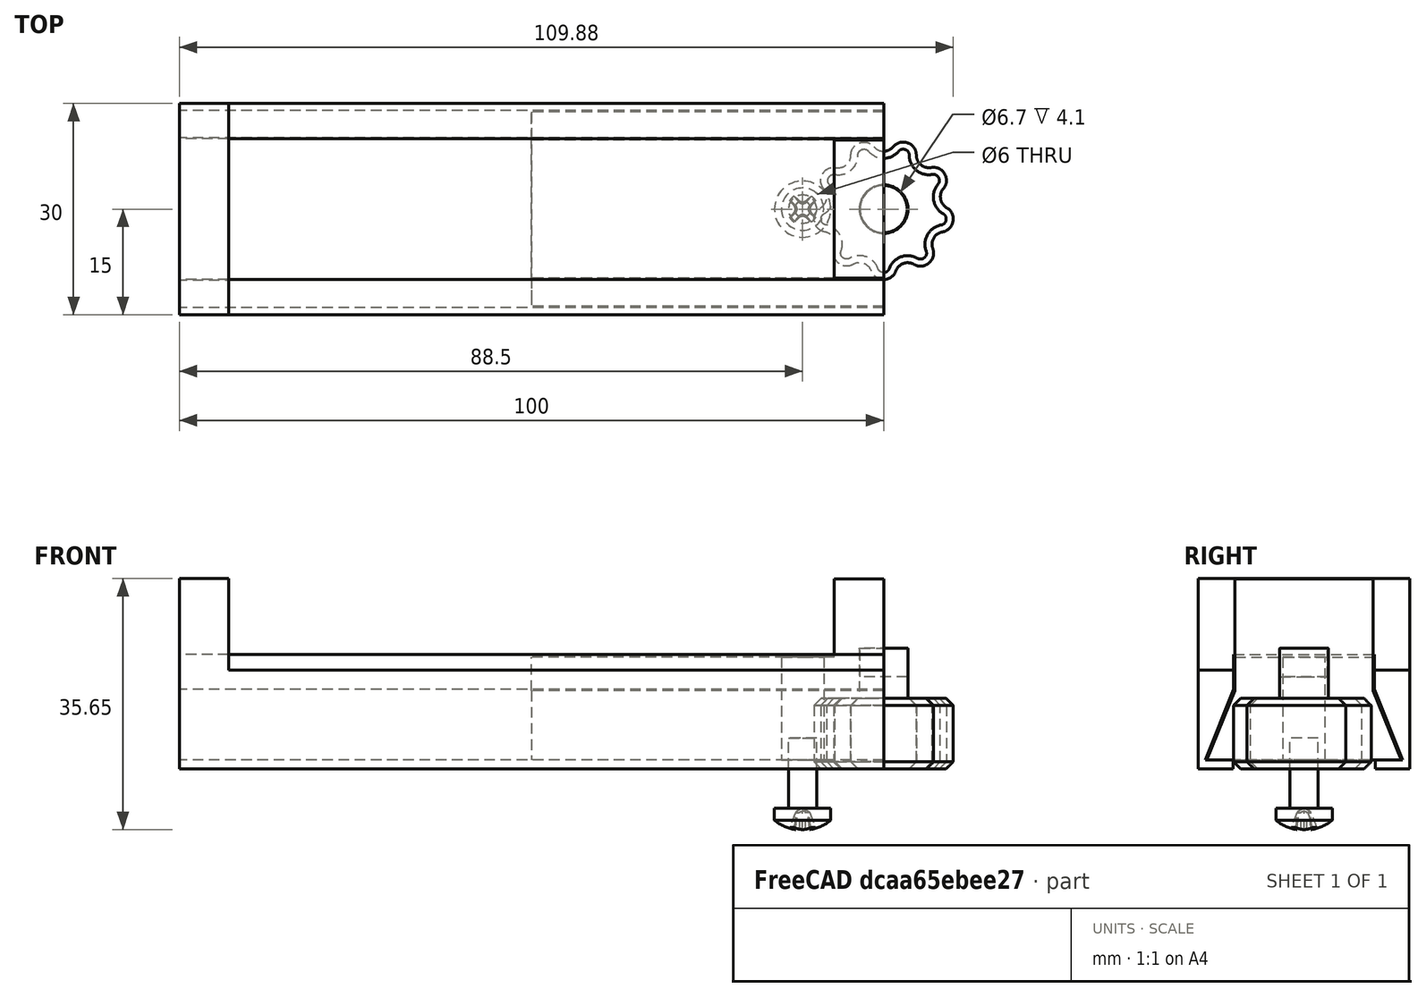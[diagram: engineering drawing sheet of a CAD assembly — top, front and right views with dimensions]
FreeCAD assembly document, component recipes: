
FREECAD ASSEMBLY — COMPONENT RECIPES ("USBCPhoneHolder - 04022025")

This assembly document has 4 components, labeled P0..P3 below (a component is one placed body or linked part). 4 of them carry a construction recipe — the FreeCAD feature program that regenerates the part from scratch, quoted from this document or its linked companion documents; the rest are supplied as boundary geometry only. No exploded tour is included for this assembly.
COMPONENT P0 — recipe-attached ("PhoneClampLeftStationary", modeled in this document).
Construction recipe (the document's own serialized feature program — sketch geometry with constraints, then the solid features built on it; lengths are millimeters unless a unit is written):

FEATURE [Sketcher::SketchObject] Sketch
  ArcFitTolerance = 1e-06
  FullyConstrained = true
  MakeInternals = false
  expr: Constraints[2] = Spreadsheet001.PhoneClampWidth
  expr: Constraints[3] = Spreadsheet001.PhoneClampHeight
  sketch-geometry (7):
    g0: LineSegment StartX=0 StartY=-15 StartZ=0 EndX=0 EndY=15 EndZ=0
    g1: LineSegment StartX=-100 StartY=15 StartZ=0 EndX=-100 EndY=-15 EndZ=0
    g2: LineSegment StartX=-93 StartY=15 StartZ=0 EndX=-93 EndY=-15 EndZ=0
    g3: LineSegment StartX=-100 StartY=15 StartZ=0 EndX=-93 EndY=15 EndZ=0
    g4: LineSegment StartX=-93 StartY=15 StartZ=0 EndX=0 EndY=15 EndZ=0
    g5: LineSegment StartX=-100 StartY=-15 StartZ=0 EndX=-93 EndY=-15 EndZ=0
    g6: LineSegment StartX=-93 StartY=-15 StartZ=0 EndX=0 EndY=-15 EndZ=0
  constraints (19):
    c: Vertical(g0)
    c: Vertical(g1)
    c: DistanceX(g1,g0) = 100
    c: DistanceY(g0,g0) = 30
    c: Symmetric(g0,g0,g-1)
    c: Vertical(g2)
    c: DistanceX(g1,g2) = 7  'LengthOfClip'
    c: Coincident(g3,g1)
    c: Coincident(g3,g2)
    c: Horizontal(g3)
    c: Coincident(g4,g2)
    c: Coincident(g4,g0)
    c: Horizontal(g4)
    c: Coincident(g5,g1)
    c: Coincident(g5,g2)
    c: Horizontal(g5)
    c: Coincident(g6,g2)
    c: Coincident(g6,g0)
    c: Horizontal(g6)
FEATURE [PartDesign::Pad] Pad
  Direction = (0,0,1)
  Length = 14
  Length2 = 10
  Profile = -> Sketch [Edge2,Edge5,Edge3,Edge7,Edge4,Edge1]
  ReferenceAxis = -> Sketch [N_Axis]
  Refine = true
  Suppressed = false
  Type = 0
  expr: Length = Spreadsheet001.PhoneClampDepth
FEATURE [PartDesign::Pad] Pad001  label="LeftBody"
  BaseFeature = -> Pad
  Direction = (0,0,1)
  Length = 27.02
  Length2 = 10
  Profile = -> Sketch [Edge6,Edge5,Edge3,Edge4]
  ReferenceAxis = -> Sketch [N_Axis]
  Refine = true
  Suppressed = false
  Type = 0
  expr: Length = Spreadsheet001.PhoneClampDepth * 1.93
FEATURE [PartDesign::Boolean] Boolean
  BaseFeature = -> Pad001
  Group = -> [Body001]
  Refine = true
  Suppressed = false
  Type = 1
  UsePlacement = true
FEATURE [Sketcher::SketchObject] Sketch007  label="BottomRemoval"
  ArcFitTolerance = 1e-06
  AttachmentSupport = -> [Boolean]
  FullyConstrained = true
  MakeInternals = false
  MapMode = 5
  Placement = pos=(0,0,0) rot=(0.57735,0.57735,0.57735;2.0944rad)
  expr: Constraints[15] = <<ProfileStationaryCut>>.Constraints.OffsetFromBottom
  expr: Constraints[16] = Spreadsheet001.KnobDiameter / 2 + Spreadsheet.PLA / 2
  sketch-geometry (6):
    g0: LineSegment StartX=0 StartY=0 StartZ=0 EndX=-10.1 EndY=0 EndZ=0
    g1: LineSegment StartX=-10.1 StartY=0 StartZ=0 EndX=-10.1 EndY=1.29 EndZ=0
    g2: LineSegment StartX=-10.1 StartY=1.29 StartZ=0 EndX=0 EndY=1.29 EndZ=0
    g3: LineSegment StartX=0 StartY=1.29 StartZ=0 EndX=10.1 EndY=1.29 EndZ=0
    g4: LineSegment StartX=10.1 StartY=1.29 StartZ=0 EndX=10.1 EndY=0 EndZ=0
    g5: LineSegment StartX=10.1 StartY=0 StartZ=0 EndX=0 EndY=0 EndZ=0
  constraints (17):
    c: Coincident(g0,g-1)
    c: PointOnObject(g0,g-1)
    c: Coincident(g1,g0)
    c: Vertical(g1)
    c: Coincident(g2,g1)
    c: PointOnObject(g2,g-2)
    c: Horizontal(g2)
    c: Coincident(g3,g2)
    c: Horizontal(g3)
    c: Coincident(g4,g3)
    c: PointOnObject(g4,g-1)
    c: Vertical(g4)
    c: Coincident(g5,g4)
    c: Coincident(g5,g0)
    c: Equal(g0,g5)
    c: DistanceY(g1,g1) = 1.29
    c: DistanceX(g0,g0) = 10.1
FEATURE [PartDesign::Pocket] Pocket001  label="HoleBottom"
  BaseFeature = -> Boolean
  Direction = (-1,0,0)
  Length = 5
  Length2 = 5
  Profile = -> Sketch007
  ReferenceAxis = -> Sketch007 [N_Axis]
  Refine = true
  Suppressed = false
  Type = 1
FEATURE [PartDesign::Body] Body  label="PhoneClampLeftStationary"
  AllowCompound = false
  Group = -> [Sketch,Pad,Pad001,Boolean,Sketch007,Pocket001]
  Origin = -> Origin
  Tip = -> Pocket001
COMPONENT P1 — recipe-attached ("PhoneClampSubtract", modeled in this document).
Construction recipe (the document's own serialized feature program — sketch geometry with constraints, then the solid features built on it; lengths are millimeters unless a unit is written):

FEATURE [Part::Part2DObjectPython] Clone2D  label="ProfileStationaryCut (2D)"  # Draft 2D object (typed FeaturePython)
  Fuse = false
  Objects = -> [Sketch002]
  Placement = pos=(0,0,0) rot=(0.57735,0.57735,0.57735;2.0944rad)
  Scale = (1,1,1)
FEATURE [PartDesign::Pad] Pad002
  Direction = (1,1e-16,-1e-16)
  Length = 100
  Length2 = 10
  Placement = pos=(0,0,0) rot=(0.57735,0.57735,0.57735;2.0944rad)
  Profile = -> Clone2D
  ReferenceAxis = -> Clone2D [N_Axis]
  Refine = true
  Reversed = true
  Suppressed = false
  Type = 0
  expr: Length = Spreadsheet001.PhoneClampWidth
FEATURE [PartDesign::Body] Body001  label="PhoneClampSubtract"
  AllowCompound = false
  Group = -> [Clone2D,Pad002]
  Origin = -> Origin001
  Tip = -> Pad002
COMPONENT P2 — recipe-attached ("PhoneClampMovable", modeled in this document).
Construction recipe (the document's own serialized feature program — sketch geometry with constraints, then the solid features built on it; lengths are millimeters unless a unit is written):

FEATURE [Part::Part2DObjectPython] Clone2D001  label="AutoRatio_ProfileMovable (2D)"  # Draft 2D object (typed FeaturePython)
  Fuse = false
  Objects = -> [Sketch003]
  Placement = pos=(0,0,0) rot=(0.57735,0.57735,0.57735;2.0944rad)
  Scale = (1,1,1)
FEATURE [PartDesign::Pad] Pad003
  Direction = (1,1e-16,-1e-16)
  Length = 50
  Length2 = 10
  Placement = pos=(0,0,0) rot=(0.57735,0.57735,0.57735;2.0944rad)
  Profile = -> Clone2D001 [Edge10,Edge1,Edge2,Edge3,Edge4,Edge5,Edge6]
  ReferenceAxis = -> Clone2D001 [N_Axis]
  Refine = true
  Reversed = true
  Suppressed = false
  Type = 0
  expr: Length = Spreadsheet001.PhoneClampWidth / 2
FEATURE [PartDesign::Pad] Pad004
  BaseFeature = -> Pad003
  Direction = (1,1e-16,-1e-16)
  Length = 7
  Length2 = 10
  Placement = pos=(0,0,0) rot=(0.57735,0.57735,0.57735;2.0944rad)
  Profile = -> Clone2D001 [Edge10,Edge9,Edge8,Edge7]
  ReferenceAxis = -> Clone2D001 [N_Axis]
  Refine = true
  Reversed = true
  Suppressed = false
  Type = 0
  expr: Length = Spreadsheet001.PhoneClampDepth / 2
FEATURE [Sketcher::SketchObject] Sketch008  label="BottomKnobHole"
  ArcFitTolerance = 1e-06
  AttachmentSupport = -> [Pad004]
  FullyConstrained = true
  MakeInternals = false
  MapMode = 5
  Placement = pos=(5e-16,-8e-16,1.29) rot=(0.707107,0.707107,0;3.14159rad)
  expr: Constraints[1] = Sketch.Constraints.LengthOfClip + 1.5 mm + Spreadsheet001.ThreadDiameter / 2
  expr: Constraints[2] = Spreadsheet001.ThreadDiameter
  sketch-geometry (1):
    g0: Circle CenterX=0 CenterY=-11.5 CenterZ=0 NormalX=0 NormalY=0 NormalZ=1 AngleXU=0 Radius=3
  constraints (3):
    c: PointOnObject(g0,g-2)
    c: DistanceY(g0,g-1) = 11.5
    c: Diameter(g0) = 6
FEATURE [PartDesign::Pocket] Pocket002  label="ThreadHole"
  BaseFeature = -> Pad004
  Direction = (0,0,1)
  Length = 5
  Length2 = 5
  Placement = pos=(0,0,0) rot=(0.57735,0.57735,0.57735;2.0944rad)
  Profile = -> Sketch008
  ReferenceAxis = -> Sketch008 [N_Axis]
  Refine = true
  Suppressed = false
  Type = 1
FEATURE [PartDesign::CoordinateSystem] LCS_Origin
  AttacherType = Attacher::AttachEngine3D
  AttachmentSupport = -> [Pocket002]
FEATURE [PartDesign::Line] HoleAxis_1
  AttacherType = Attacher::AttachEngineLine
  AttachmentSupport = -> [Pocket002]
  Length = 8.20244
  MapMode = 19
  Placement = pos=(-11.5,-4e-15,1.29) rot=(0.707107,0.707107,0;3.14159rad)
  ResizeMode = 1
FEATURE [PartDesign::Body] Body002  label="PhoneClampMovable"
  AllowCompound = false
  Group = -> [Clone2D001,Pad003,Pad004,Sketch008,Pocket002,LCS_Origin,HoleAxis_1]
  Origin = -> Origin002
  Tip = -> Pocket002
COMPONENT P3 — recipe-attached ("Knob", modeled in this document).
Construction recipe (the document's own serialized feature program — sketch geometry with constraints, then the solid features built on it; lengths are millimeters unless a unit is written):

FEATURE [Sketcher::SketchObject] Sketch004
  ArcFitTolerance = 1e-06
  AttachmentSupport = -> [XY_Plane003]
  FullyConstrained = true
  MakeInternals = false
  MapMode = 5
  expr: Constraints[1] = Spreadsheet001.KnobDiameter
  sketch-geometry (1):
    g0: Circle CenterX=0 CenterY=0 CenterZ=0 NormalX=0 NormalY=0 NormalZ=1 AngleXU=0 Radius=10
  constraints (2):
    c: Coincident(g0,g-1)
    c: Diameter(g0) = 20
FEATURE [PartDesign::Pad] Pad005  label="Knob Body Pad"
  Direction = (0,0,1)
  Length = 10
  Length2 = 10
  Profile = -> Sketch004
  ReferenceAxis = -> Sketch004 [N_Axis]
  Refine = true
  Suppressed = false
  Type = 0
FEATURE [Sketcher::SketchObject] Sketch005  label="KnurelCutSketch"
  ArcFitTolerance = 1e-06
  AttachmentSupport = -> [Pad005]
  ExternalGeometry = -> [Pad005]
  FullyConstrained = false
  MakeInternals = false
  MapMode = 5
  Placement = pos=(0,0,10) rot=(0,0,1;0rad)
  expr: Constraints[0] = Spreadsheet001.KnobDiameter * 5 / 28
  sketch-geometry (1):
    g0: Circle CenterX=0 CenterY=10 CenterZ=0 NormalX=0 NormalY=0 NormalZ=1 AngleXU=0 Radius=1.78571
  constraints (2):
    c: Diameter(g0) = 3.57143
    c: PointOnObject(g0,g-3)
FEATURE [PartDesign::Pocket] Pocket  label="KnurelPocket"
  BaseFeature = -> Pad005
  Direction = (0,0,-1)
  Length = 5
  Length2 = 5
  Profile = -> Sketch005
  ReferenceAxis = -> Sketch005 [N_Axis]
  Refine = true
  Suppressed = false
  Type = 1
FEATURE [PartDesign::PolarPattern] PolarPattern
  Angle = 360
  Axis = -> Sketch005 [N_Axis]
  BaseFeature = -> Pocket
  Mode = 0
  Occurrences = 9
  Offset = 120
  Originals = -> [Pocket]
  Refine = true
  Suppressed = false
  TransformMode = 0
FEATURE [Sketcher::SketchObject] Sketch006  label="Stand off Sketch"
  ArcFitTolerance = 1e-06
  AttachmentSupport = -> [PolarPattern]
  FullyConstrained = true
  MakeInternals = false
  MapMode = 5
  Placement = pos=(0,0,10) rot=(0,0,1;0rad)
  expr: .Constraints.BottomHoleMM = Spreadsheet001.ScrewHeadWidth + Spreadsheet.PLA * 2
  sketch-geometry (1):
    g0: Circle CenterX=0 CenterY=0 CenterZ=0 NormalX=0 NormalY=0 NormalZ=1 AngleXU=0 Radius=3.45
  constraints (2):
    c: Coincident(g0,g-1)
    c: Diameter(g0) = 6.9  'BottomHoleMM'
FEATURE [PartDesign::Pad] Pad006  label="Stand off Pad"
  BaseFeature = -> PolarPattern
  Direction = (0,0,1)
  Length = 7.14286
  Length2 = 10
  Profile = -> Sketch006
  ReferenceAxis = -> Sketch006 [N_Axis]
  Refine = true
  Suppressed = false
  Type = 0
  expr: Length = Spreadsheet001.KnobDiameter * 10 / 28
FEATURE [PartDesign::Fillet] Fillet
  Base = -> Pad006 [Edge33,Edge34,Edge37,Edge38,Edge41,Edge42,Edge45,Edge46,Edge49,Edge50,Edge53,Edge21,Edge20,Edge22,Edge25,Edge26,Edge29,Edge30]
  BaseFeature = -> Pad006
  Radius = 1.8
  Refine = true
  SupportTransform = false
  Suppressed = false
  UseAllEdges = false
FEATURE [PartDesign::Chamfer] Chamfer
  Angle = 45
  Base = -> Fillet [Edge16,Edge37]
  BaseFeature = -> Fillet
  ChamferType = 0
  FlipDirection = false
  Refine = true
  Size = 1
  Size2 = 1
  SupportTransform = false
  Suppressed = false
  UseAllEdges = false
FEATURE [PartDesign::CoordinateSystem] LCS_Knob
  AttacherType = Attacher::AttachEngine3D
FEATURE [Sketcher::SketchObject] Sketch009
  ArcFitTolerance = 1e-06
  AttachmentSupport = -> [Chamfer]
  FullyConstrained = true
  MakeInternals = false
  MapMode = 5
  Placement = pos=(0,0,17.1429) rot=(0,0,1;0rad)
  expr: Constraints[1] = <<Stand off Sketch>>.Constraints.BottomHoleMM - Spreadsheet.PLA
  sketch-geometry (1):
    g0: Circle CenterX=0 CenterY=0 CenterZ=0 NormalX=0 NormalY=0 NormalZ=1 AngleXU=0 Radius=3.35
  constraints (2):
    c: Coincident(g0,g-1)
    c: Diameter(g0) = 6.7
FEATURE [PartDesign::Pocket] Pocket003  label="ScrewHeadPocket"
  BaseFeature = -> Chamfer
  Direction = (0,0,-1)
  Length = 4.1
  Length2 = 5
  Profile = -> Sketch009
  ReferenceAxis = -> Sketch009 [N_Axis]
  Refine = true
  Suppressed = false
  Type = 0
  expr: Length = Spreadsheet001.ScrewHeadHeight + Spreadsheet.PLA
FEATURE [PartDesign::Fillet] Fillet001
  Base = -> Pocket003 [Edge255]
  BaseFeature = -> Pocket003
  Radius = 0.087
  Refine = true
  SupportTransform = false
  Suppressed = false
  UseAllEdges = false
FEATURE [Sketcher::SketchObject] Sketch010  label="VisibleTestAlignmentSketch"
  ArcFitTolerance = 1e-06
  AttachmentSupport = -> [Fillet001]
  FullyConstrained = false
  MakeInternals = false
  MapMode = 5
  Placement = pos=(0,0,13.0429) rot=(0,0,1;0rad)
  sketch-geometry (1):
    g0: Circle CenterX=0 CenterY=0 CenterZ=0 NormalX=0 NormalY=0 NormalZ=1 AngleXU=0 Radius=4.56138
  constraints (1):
    c: Coincident(g0,g-1)
FEATURE [PartDesign::Body] Body003  label="Knob"
  AllowCompound = false
  Group = -> [Sketch004,Pad005,Sketch005,Pocket,PolarPattern,Sketch006,Pad006,Fillet,Chamfer,LCS_Knob,Sketch009,Pocket003,Fillet001,Sketch010]
  Origin = -> Origin003
  Tip = -> Fillet001
PROVENANCE & LICENSES
A FreeCAD (.FCStd) document from a public repository crawl; recipes are the document's own serialized feature recipes (and, for linked parts, companion documents' recipes).
License: as declared in the source repository (recorded in the dataset sidecar).
